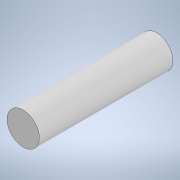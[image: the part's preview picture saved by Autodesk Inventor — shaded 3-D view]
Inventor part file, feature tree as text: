
AUTODESK INVENTOR PART (.ipt)
format: ipt  version: 2021 (Build 250183000, 183)  size: 89,088 bytes
history: native  units: mm
features: extrude x1, sketch x1
ambient origin geometry x8: Origin, YZ Plane, XZ Plane, XY Plane, X Axis, Y Axis, Z Axis, Center Point
bodies: Solid1 (feature_tree)
feature tree (2):
  extrude  "Extrusion1"  Depth=207.0mm TaperAngle=0.0deg
  sketch  "Sketch1"  dims[d0=50.0mm d1=207.0mm d2=0.0mm]
